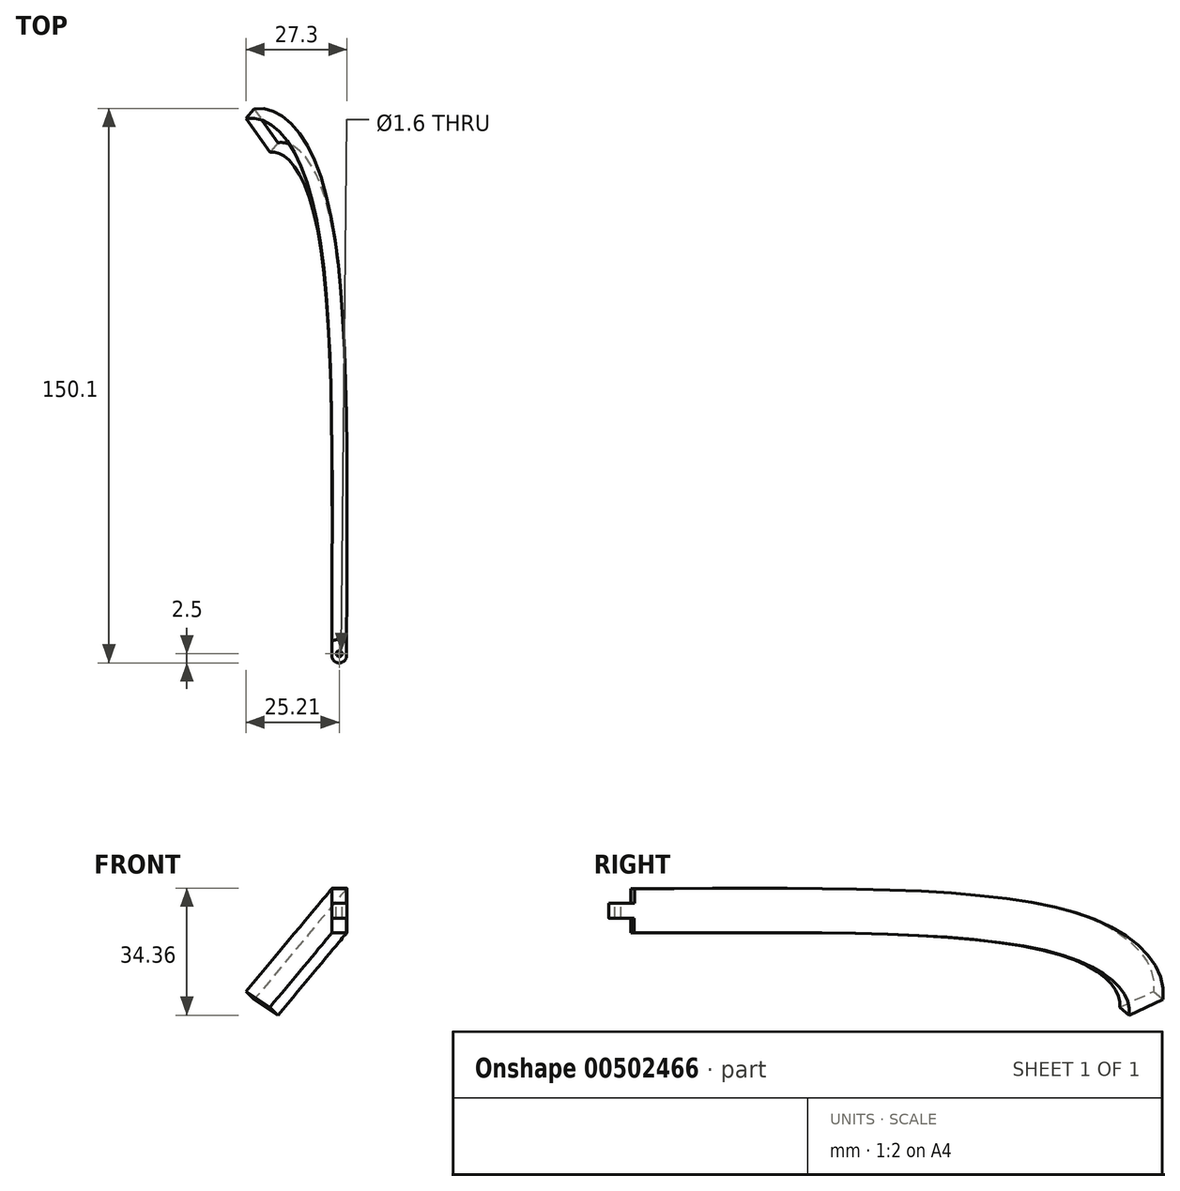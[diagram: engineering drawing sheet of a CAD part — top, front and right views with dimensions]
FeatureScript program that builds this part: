
annotation { "Feature Type Name" : "Feature", "Feature Type Description" : "" }
export const myFeature = defineFeature(function(context is Context, id is Id, definition is map)
    precondition{}
    {
        {
            var Q0;
            Q0=qCreatedBy(makeId("Top.planeOp"),FACE);
            var sketch = newSketch(context, id + "F0", { "sketchPlane" : qUnion([Q0])});
            skLineSegment(sketch, "E0", {"start": v(0, 0) * mm, "end": v(0, 150) * mm, "construction": true});
            skLineSegment(sketch, "E1", {"start": v(0, 150) * mm, "end": v(-25, 150) * mm, "construction": true});
            skFitSpline(sketch, "E2", {"points": [v(0, 0) * mm, v(-6.36, 109.15) * mm, v(-25, 150) * mm], "startDerivative": vector(-6.68, 178.45) * mm, "endDerivative": vector(-47.83, 54) * mm});
            skSolve(sketch);
        }
        {
            var Q0;
            Q0=qCreatedBy(makeId("Right.planeOp"),FACE);
            var sketch = newSketch(context, id + "F1", { "sketchPlane" : qUnion([Q0])});
            skFitSpline(sketch, "E3.0", {"points": [v(0, 0) * mm, v(36.25, 0) * mm, v(106.12, 0) * mm, v(142.97, 0) * mm, v(150, 0) * mm]});
            skLineSegment(sketch, "E4", {"start": v(150, 0) * mm, "end": v(150, -30) * mm, "construction": true});
            skFitSpline(sketch, "E5", {"points": [v(0, 0) * mm, v(127.37, -8.38) * mm, v(150, -30) * mm], "startDerivative": vector(246.98, 0) * mm, "endDerivative": vector(21.75, -76.1) * mm});
            skSolve(sketch);
        }
        {
            var Q0;
            Q0=qCreatedBy(makeId("Front.planeOp"),FACE);
            var Q1;
            Q1=sQuery(id+"F1.wireOp",VERTEX,"E3.0.end");
            cPlane(context, id + "F2", {"entities" : qUnion([Q0, Q1]), "cplaneType" : CPlaneType.PLANE_POINT, "offset" : 25 * mm, "width" : 150 * mm, "height" : 150 * mm});
        }
        {
            var Q0;
            Q0=qCreatedBy(id+"F2.planeOp",FACE);
            var sketch = newSketch(context, id + "F3", { "sketchPlane" : qUnion([Q0])});
            skPoint(sketch, "E6.0", {"position": v(-25, 0) * mm});
            skPoint(sketch, "E6.1", {"position": v(0, -30) * mm});
            skLineSegment(sketch, "E7", {"start": v(-25, 0) * mm, "end": v(-25, -30) * mm});
            skLineSegment(sketch, "E8", {"start": v(-25, -30) * mm, "end": v(0, -30) * mm});
            skSolve(sketch);
        }
        {
            var Q0;
            Q0=sQuery(id+"F1.wireOp",VERTEX,"E3.0.start");
            var Q1;
            Q1=sQuery(id+"F1.wireOp",VERTEX,"E3.0.end");
            var Q2;
            Q2=sQuery(id+"F3.wireOp",VERTEX,"E8.start");
            cPlane(context, id + "F4", {"entities" : qUnion([Q0, Q1, Q2]), "cplaneType" : CPlaneType.THREE_POINT, "offset" : 25 * mm, "width" : 150 * mm, "height" : 150 * mm});
        }
        {
            var Q0;
            Q0=qCreatedBy(id+"F4.planeOp",FACE);
            var sketch = newSketch(context, id + "F5", { "sketchPlane" : qUnion([Q0])});
            skPoint(sketch, "E9.0", {"position": v(150, -39.05) * mm});
            skPoint(sketch, "E10.0", {"position": v(0, 0) * mm});
            skFitSpline(sketch, "E11", {"points": [v(0, 0) * mm, v(132.06, -11.11) * mm, v(150, -39.05) * mm], "startDerivative": vector(257.6, 0) * mm, "endDerivative": vector(-9.04, -95.5) * mm});
            skSolve(sketch);
        }
        {
            var Q0;
            Q0=qCreatedBy(makeId("Front.planeOp"),FACE);
            var sketch = newSketch(context, id + "F6", { "sketchPlane" : qUnion([Q0])});
            skLineSegment(sketch, "E12", {"start": v(0, 0) * mm, "end": v(0, -12) * mm});
            skLineSegment(sketch, "E13", {"start": v(0, -12) * mm, "end": v(-4, -12) * mm});
            skLineSegment(sketch, "E14", {"start": v(-4, -12) * mm, "end": v(-4, 0) * mm});
            skLineSegment(sketch, "E15", {"start": v(-4, 0) * mm, "end": v(0, 0) * mm});
            skSolve(sketch);
        }
        {
            var Q0;
            Q0=makeQuery(id+"F6.imprint","IMPRINT",FACE,{"disambiguationData":[TD([[makeQuery(id+"F6.imprint","IMPRINT",EDGE,{"derivedFrom":sQuery(id+"F6.wireOp",EDGE,"E12")}),-1.0]])]});
            var Q1;
            Q1=sQuery(id+"F5.wireOp",EDGE,"E11");
            sweep(context, id + "F7", {"profiles" : qUnion([Q0]), "path" : qUnion([Q1])});
        }
        {
            var Q0;
            Q0=makeQuery(id+"F7.opSweep","CAP_FACE",FACE,{"disambiguationData":[OSD([sQuery(id+"F5.wireOp",VERTEX,"E11.start"),sQuery(id+"F6.wireOp",EDGE,"E12"),sQuery(id+"F6.wireOp",EDGE,"E13"),sQuery(id+"F6.wireOp",EDGE,"E14"),sQuery(id+"F6.wireOp",EDGE,"E15")])],"isStart":true});
            var sketch = newSketch(context, id + "F8", { "sketchPlane" : qUnion([Q0])});
            skLineSegment(sketch, "E16", {"start": v(-4, 0) * mm, "end": v(-4, -4) * mm, "construction": true});
            skLineSegment(sketch, "E17", {"start": v(-4, -4) * mm, "end": v(0, -4) * mm});
            skLineSegment(sketch, "E18", {"start": v(0, -4) * mm, "end": v(0, -8) * mm});
            skLineSegment(sketch, "E19", {"start": v(0, -8) * mm, "end": v(-4, -8) * mm});
            skSolve(sketch);
        }
        {
            var Q0;
            Q0=qCreatedBy(makeId("Top.planeOp"),FACE);
            var sketch = newSketch(context, id + "F9", { "sketchPlane" : qUnion([Q0])});
            skLineSegment(sketch, "E20", {"start": v(0, 0) * mm, "end": v(0, 2.5) * mm, "construction": true});
            skLineSegment(sketch, "E21", {"start": v(0, 2.5) * mm, "end": v(-4, 2.5) * mm, "construction": true});
            skCircle(sketch, "E22", {"center": v(-2, 2.5) * mm, "radius": 0.8 * mm});
            skSolve(sketch);
        }
        {
            var Q0;
            Q0 = qSketchRegion(id + "F9", true);
            var Q1;
            Q1=sQuery(id+"F9.wireOp",EDGE,"E22");
            extrude(context, id + "F10", {"entities" : qUnion([Q0]), "operationType" : NewBodyOperationType.REMOVE, "surfaceEntities" : qUnion([Q1]), "oppositeDirection" : true, "depth" : 25 * mm, "offsetDistance" : 25 * mm, "hasSecondDirection" : true, "secondDirectionOppositeDirection" : false, "secondDirectionDepth" : 2.5 * mm});
        }
        {
            var Q0;
            {var subQ0=sQuery(id+"F8.wireOp",EDGE,"E17");Q0=makeQuery(id+"F8.imprint","IMPRINT",FACE,{"disambiguationData":[TD([[makeQuery(id+"F8.imprint","IMPRINT",EDGE,{"derivedFrom":subQ0}),1.0]])]});}
            var Q1;
            {var subQ0=sQuery(id+"F8.wireOp",EDGE,"E19");Q1=makeQuery(id+"F8.imprint","IMPRINT",FACE,{"disambiguationData":[TD([[makeQuery(id+"F8.imprint","IMPRINT",EDGE,{"derivedFrom":subQ0}),1.0]])]});}
            extrude(context, id + "F11", {"entities" : qUnion([Q0, Q1]), "operationType" : NewBodyOperationType.REMOVE, "oppositeDirection" : true, "depth" : (6.5 - 0.55) * mm, "offsetDistance" : 25 * mm});
        }
        {
            var Q0;
            Q0=qCreatedBy(makeId("Top.planeOp"),FACE);
            var sketch = newSketch(context, id + "F12", { "sketchPlane" : qUnion([Q0])});
            skPoint(sketch, "E23.0", {"position": v(-4, 5.95) * mm});
            skLineSegment(sketch, "E24", {"start": v(-4, 5.95) * mm, "end": v(0, 5.95) * mm});
            skLineSegment(sketch, "E25", {"start": v(-4, 5.95) * mm, "end": v(1.04, 7.3) * mm});
            skLineSegment(sketch, "E26", {"start": v(0, 5.95) * mm, "end": v(0, 7.02) * mm});
            skSolve(sketch);
        }
        {
            var Q0;
            Q0 = qSketchRegion(id + "F12", true);
            extrude(context, id + "F13", {"entities" : qUnion([Q0]), "operationType" : NewBodyOperationType.REMOVE, "oppositeDirection" : true, "depth" : 4 * mm, "offsetDistance" : 25 * mm});
        }
        {
            var Q0;
            Q0=qCreatedBy(makeId("Top.planeOp"),FACE);
            cPlane(context, id + "F14", {"entities" : qUnion([Q0]), "cplaneType" : CPlaneType.OFFSET, "offset" : 12 * mm, "oppositeDirection" : true, "width" : 150 * mm, "height" : 150 * mm});
        }
        {
            var Q0;
            Q0=qCreatedBy(id+"F14.planeOp",FACE);
            var sketch = newSketch(context, id + "F15", { "sketchPlane" : qUnion([Q0])});
            skPoint(sketch, "E27.0", {"position": v(0, 5.95) * mm});
            skLineSegment(sketch, "E28", {"start": v(0, 5.95) * mm, "end": v(-4, 5.95) * mm});
            skLineSegment(sketch, "E29.MirrorCS", {"start": v(0, 6.88) * mm, "end": v(0, 5.95) * mm});
            skLineSegment(sketch, "E30.MirrorCS", {"start": v(-4, 5.95) * mm, "end": v(0, 6.88) * mm});
            skSolve(sketch);
        }
        {
            var Q0;
            {var subQ0=sQuery(id+"F15.wireOp",EDGE,"E28");Q0=makeQuery(id+"F15.imprint","IMPRINT",FACE,{"disambiguationData":[TD([[makeQuery(id+"F15.imprint","IMPRINT",EDGE,{"derivedFrom":subQ0}),-1.0]])]});}
            extrude(context, id + "F16", {"entities" : qUnion([Q0]), "operationType" : NewBodyOperationType.REMOVE, "depth" : 4 * mm, "offsetDistance" : 25 * mm});
        }
        {
            var Q0;
            Q0=makeQuery(id+"F7.opSweep","CAP_EDGE",EDGE,{"disambiguationData":[OSD([sQuery(id+"F5.wireOp",VERTEX,"E11.start"),sQuery(id+"F6.wireOp",EDGE,"E14")])],"isStart":true});
            var Q1;
            Q1=makeQuery(id+"F7.opSweep","CAP_EDGE",EDGE,{"disambiguationData":[OSD([sQuery(id+"F5.wireOp",VERTEX,"E11.start"),sQuery(id+"F6.wireOp",EDGE,"E12")])],"isStart":true});
            fillet(context, id + "F17", {"entities" : qUnion([Q0, Q1]), "radius" : 2 * mm, "tangentPropagation" : true, "allowEdgeOverflow" : false});
        }
    });
